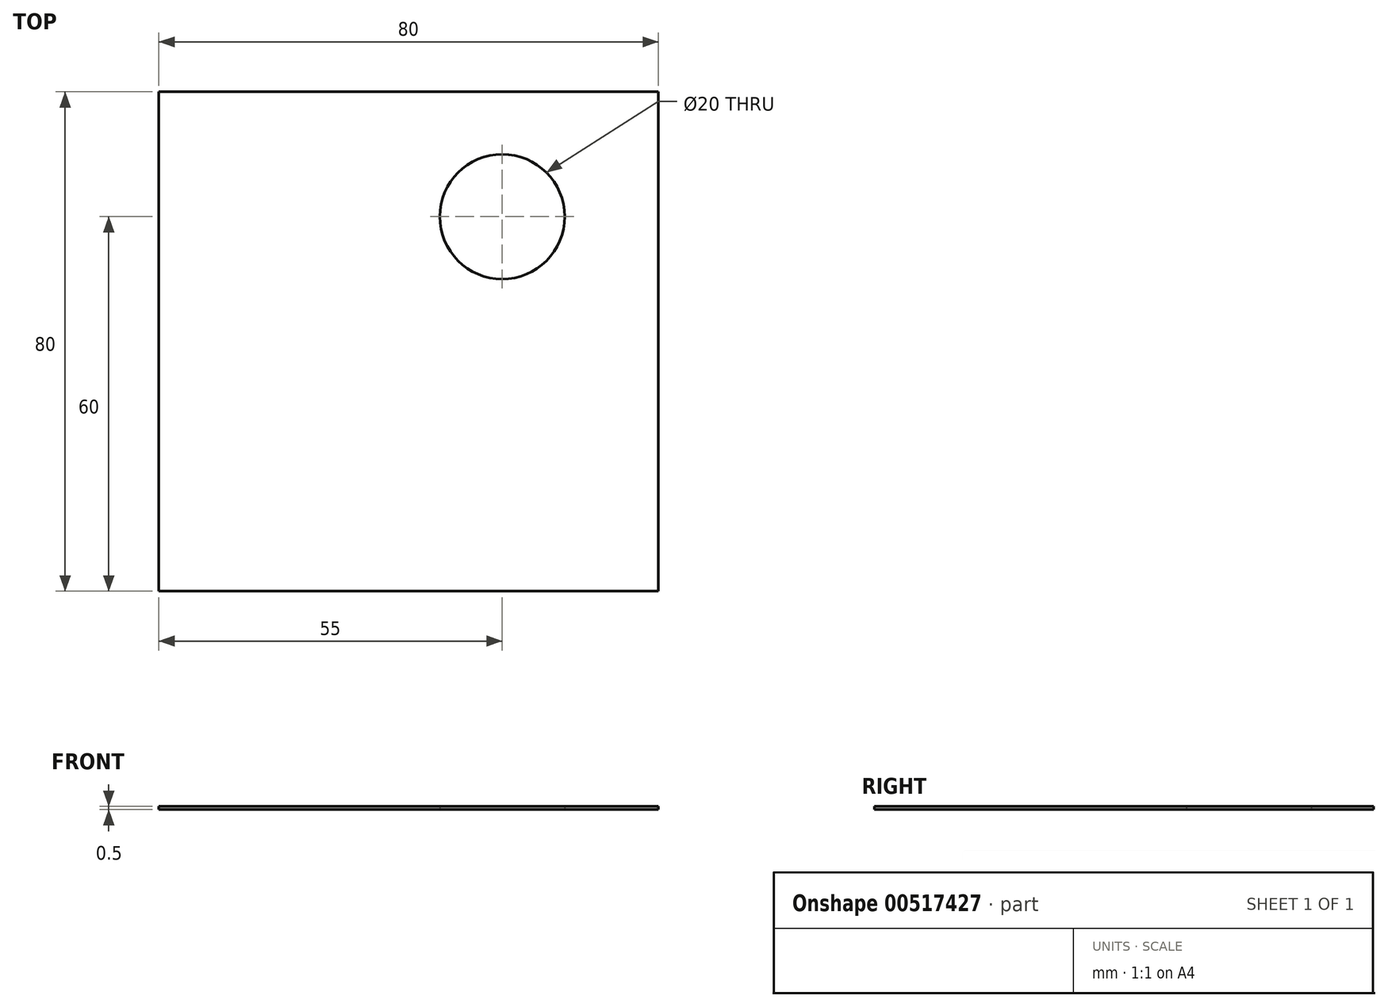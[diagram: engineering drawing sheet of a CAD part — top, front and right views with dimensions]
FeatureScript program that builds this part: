
annotation { "Feature Type Name" : "Feature", "Feature Type Description" : "" }
export const myFeature = defineFeature(function(context is Context, id is Id, definition is map)
    precondition{}
    {
        {
            var Q0;
            Q0=qCreatedBy(makeId("Top.planeOp"),FACE);
            var sketch = newSketch(context, id + "F0", { "sketchPlane" : qUnion([Q0])});
            skLineSegment(sketch, "E0.bottom", {"start": v(-40, 40) * mm, "end": v(40, 40) * mm});
            skLineSegment(sketch, "E0.top", {"start": v(-40, -40) * mm, "end": v(40, -40) * mm});
            skLineSegment(sketch, "E0.left", {"start": v(-40, 40) * mm, "end": v(-40, -40) * mm});
            skLineSegment(sketch, "E0.right", {"start": v(40, 40) * mm, "end": v(40, -40) * mm});
            skPoint(sketch, "E0.middle", {"position": v(0, 0) * mm});
            skCircle(sketch, "E1", {"center": v(15, 20) * mm, "radius": 10 * mm});
            skSolve(sketch);
        }
        {
            var Q0;
            Q0=makeQuery(id+"F0.imprint","IMPRINT",FACE,{"disambiguationData":[TD([[makeQuery(id+"F0.imprint","IMPRINT",EDGE,{"derivedFrom":sQuery(id+"F0.wireOp",EDGE,"E0.bottom")}),-1.0]])]});
            extrude(context, id + "F1", {"entities" : qUnion([Q0]), "depth" : 0.5 * mm, "offsetDistance" : 25 * mm});
        }
    });
